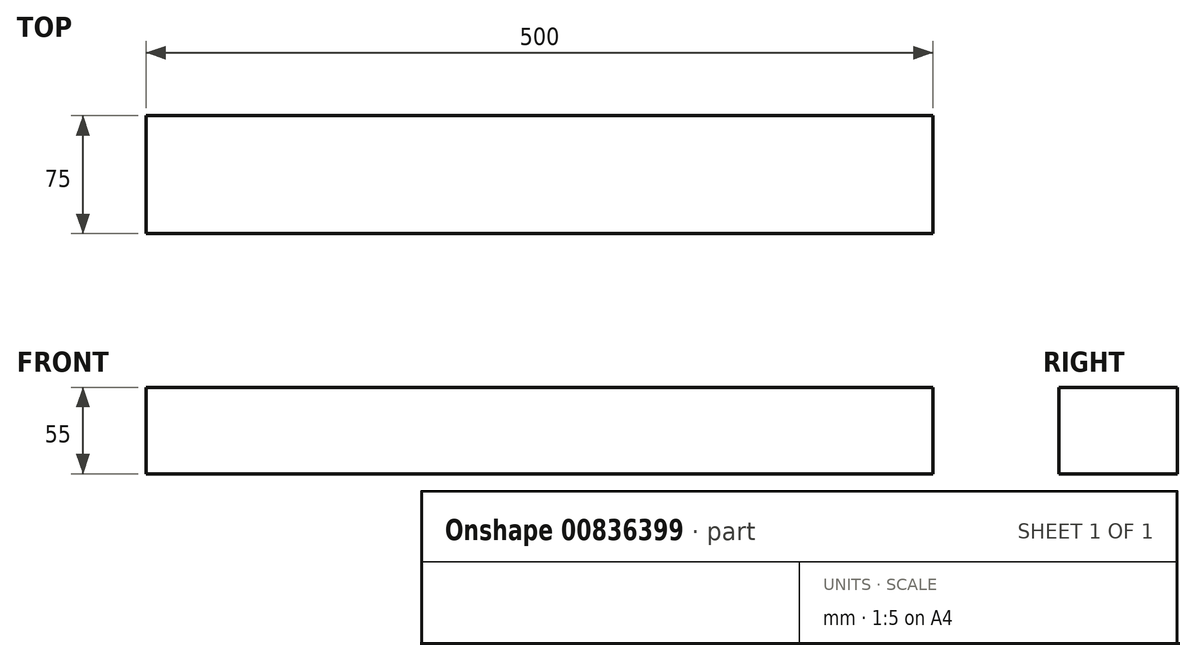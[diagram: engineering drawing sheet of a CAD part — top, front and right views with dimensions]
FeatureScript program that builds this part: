
annotation { "Feature Type Name" : "Feature", "Feature Type Description" : "" }
export const myFeature = defineFeature(function(context is Context, id is Id, definition is map)
    precondition{}
    {
        {
            var Q0;
            Q0=qCreatedBy(makeId("Right.planeOp"),FACE);
            var sketch = newSketch(context, id + "F0", { "sketchPlane" : qUnion([Q0])});
            skLineSegment(sketch, "E0.bottom", {"start": v(0, 0) * mm, "end": v(75, 0) * mm});
            skLineSegment(sketch, "E0.top", {"start": v(0, 55) * mm, "end": v(75, 55) * mm});
            skLineSegment(sketch, "E0.left", {"start": v(0, 0) * mm, "end": v(0, 55) * mm});
            skLineSegment(sketch, "E0.right", {"start": v(75, 0) * mm, "end": v(75, 55) * mm});
            skSolve(sketch);
        }
        {
            var Q0;
            Q0=makeQuery(id+"F0.imprint","IMPRINT",FACE,{"disambiguationData":[TD([[makeQuery(id+"F0.imprint","IMPRINT",EDGE,{"derivedFrom":sQuery(id+"F0.wireOp",EDGE,"E0.bottom")}),1.0]])]});
            extrude(context, id + "F1", {"entities" : qUnion([Q0]), "depth" : 500 * mm, "offsetDistance" : 25 * mm});
        }
    });
